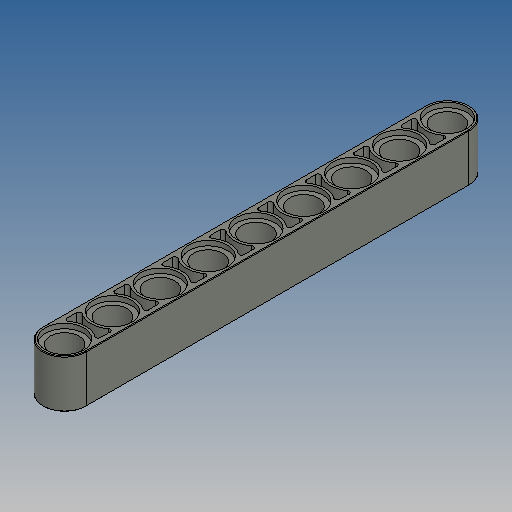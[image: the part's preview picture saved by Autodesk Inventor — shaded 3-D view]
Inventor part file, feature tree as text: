
AUTODESK INVENTOR PART (.ipt)
format: ipt  version: 2025 (Build 290162010, 162A)  size: 432,640 bytes
history: native  units: mm
features: extrude x3, sketch x3, mirror x1, fillet x1
ambient origin geometry x8: Origin, YZ Plane, XZ Plane, XY Plane, X Axis, Y Axis, Z Axis, Center Point
bodies: Solid1 (feature_tree)
feature tree (8):
  extrude  "Extrusion1"  Depth=7.2mm
  sketch  "Sketch6"  dims[d48=64.0mm d49=6.4mm d50=4.8mm d52=0.8mm d53=80.0mm d55=8.0mm d56=10.0mm d58=10.0mm d60=0.4mm d61=0.1mm]
  extrude  "Extrusion7"  Depth=3.1mm TaperAngle=0.0deg
  extrude  "Extrusion8"  Depth=6.4mm
  mirror  "Mirror1"
  fillet  "Fillet2"  Radius=4.8mm
  sketch  "Sketch1"  dims[d14=8.0mm d15=0.0mm d32=7.2mm]
  sketch  "Skizze - Rechteckige Anordnung1"  dims[d41=0.8mm d42=0.0mm d43=3.1mm d44=0.0mm]
